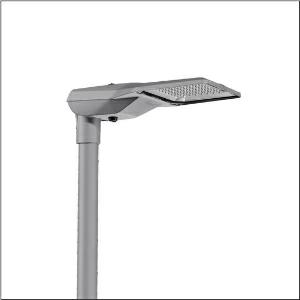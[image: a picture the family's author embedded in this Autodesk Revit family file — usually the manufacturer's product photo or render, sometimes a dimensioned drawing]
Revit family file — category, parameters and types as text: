
# Revit family: streetlight_sl_21_iq_midi___st1_0a_5xe3d21y08nb_2a15
name_source: partatom
category: Lighting Fixtures
units: mm (PartAtom-declared; Revit-internal decimal feet)

## family parameters
Cut with Voids When Loaded = No
Host = Face
Light Source = No
Part Type = Normal
Room Calculation Point = No
Round Connector Dimension = Use Diameter
Shared = No

## types (1)
- --- (1 x LED, 17280 lm, 136.6 W, 2200K)
    Apparent Load = 137 VA
    CIE Flux Codes = 40 73 97 100 100
    Color Rendering = 70
    Color Temperature = 2200K
    Default Elevation = 1800 mm
    Description = Streetlight SL 21 iQ midi, mast luminaire, primary light control with lens, of PMMA, primary optical cover: cover, of toughened safety glass, transparent, light distribution: ST1.0a, light emission: direct distribution, primary light characteristic: asymmetric, installation type: post-top, side-entry, LED, High Power LED, rated luminous flux: 17.280lm, luminous efficacy: 127lm/W, light colour: 722, colour temperature: 2200K, control: pre-setting: logarithmic dimming characteristic, Street-Remote, Auto-Match, Temp-Guard, Lumen-Switch, Night-Set, Smart-Wire, Light-Fading, Desk-Remote (wireless, voltage-free reading and setting of iQ features in the workshop via application-optimized NFC function/RFID function), optimised constant luminous flux control (CLO 2.0), mains connection: 230..240V, AC, 50/60Hz, start of lifetime: 137W, end of service life: 144W, reduction: 61W, luminaire housing, of diecast aluminium, powder-coated, Siteco® metallic grey (DB 702S), corrosivity category C5 mid according to DIN EN ISO 12944, please order mast flange separately, inclination adjustable: 0°, 5°, 10°, 15°, sealing non-destructively replaceable, multi-level sealing system, length: 644mm, width: 335mm, height: 110mm, mast flange for spigot size: 42mm (side-entry): 5XC10008XM4, 60/48mm (side-entry/post-top): 5XC10108XM2, 76/60mm (side-entry/post-top): 5XC10108XM1, Smart Interface below and above, protection rating (complete): IP66, insulation class (complete): insulation class II (safety insulation), certification: CE, ENEC, ENEC+, VDE, impact resistance: IK09, permissible operating ambient temperature for outdoor applications: -40..+50°C, standard-compliant lighting for roads and squares, packaging unit: 1 piece

Light Distribution: ST1.0a
    Height = 111 mm
    Lamp = 1 x LED
    Lamp Light Flux = 17280 lm
    Lamp Power = 136.6 W
    Lamp count = 1
    Length = 644 mm
    Luminous efficacy = 127 lm/W
    Manufacturer = Siteco
    ModVariant = No
    Model = 5XE3D21Y08NB
    Number of Poles = 1
    OnlyDefault = Yes
    Power Factor = 1
    Product Name = Streetlight SL 21 iQ midi | ST1.0a
    Product group = mast luminaire | pylon top
    ProductGroupID = 6100
    Protection Class = Protection class II
    Protection Degree = IP 66
    RLX_Detail_Level = 1
    RLX_Emergency_Light_Flux = 0 lm
    RLX_Emergency_Type = 0
    RLX_Emergency_Type_DB = No
    RlxData = <blob elided: 91093 chars, md5=cf55d1e6>
    Socket = socket
    Standby Power = 0 W
    System Light Flux = 17280 lm
    System Power = 137 W
    Type Comments = factory setting: luminous flux: 100 % | dim-lin: 254 | 733 mA
    Type Image = l_1004304.jpg
    URL = http://relux.com
    VarID = @adj_082729
    Voltage = 0 V
    Weight = 0.00 kg
    Width = 336 mm

## geometry (parser evidence)
native form markers: Blend x4, Sweep x13
no freeform markers — native parametric forms only
